# Revit family: Door-Access-Best Access Doors-Insulated-All_Surface_Types-Drywall_Flange-(BA-FRI-DF)
name_source: partatom
category: Specialty Equipment
revit_build: Autodesk Revit 2017 (Build: 20160225_1515(x64)
units: mm (PartAtom-declared; Revit-internal decimal feet)

## family parameters
Cut with Voids When Loaded = No
Host = Face
OmniClass Number = 23.30.10.27.17
Part Type = Normal
Room Calculation Point = No
Round Connector Dimension = Use Diameter
Shared = No

## types (17) — shared parameters
Assembly Code = C1020700
Ceiling Constraint = Maximum dimensions for ceiling mounted panels are 24W x 36H.
Ceiling Mounted = No
Construction Material = Metal - Best Access Doors - Aluminum
Default Elevation = 0"
Description = Fire rated insulated access door with drywall flange
Finish = Metal - Best Access Doors - Powder Coated White
Frame Depth = 2 1/4"
Manufacturer = Best Access Doors
Model = BA-FRI-DF
Product data url = https://bimobject.com
URL = https://www.bestaccessdoors.com
Wall Mounted = Yes

## per-type parameters (varying)
| type | Door Height | Door Height Calc | Door Width | Door Width Calc | Height Actual | Width Actual |
| 8 x 8 | 8" | 8" | 8" | 8" | 10 5/8" | 10 5/8" |
| Custom | 24" | 24" | 24" | 24" | 26 5/8" | 26 5/8" |
| 48 x 48 | 48" | 48" | 48" | 48" | 50 5/8" | 50 5/8" |
| 36 x 36 | 36" | 36" | 36" | 36" | 38 5/8" | 38 5/8" |
| 32 x 32 | 32" | 32" | 32" | 32" | 34 5/8" | 34 5/8" |
| 30 x 30 | 30" | 30" | 30" | 30" | 32 5/8" | 32 5/8" |
| 24 x 48 | 48" | 48" | 24" | 24" | 50 5/8" | 26 5/8" |
| 24 x 36 | 36" | 36" | 24" | 24" | 38 5/8" | 26 5/8" |
| 24 x 24 | 24" | 24" | 24" | 24" | 26 5/8" | 26 5/8" |
| 22 x 36 | 36" | 36" | 22" | 22" | 38 5/8" | 24 5/8" |
| 22 x 30 | 30" | 30" | 22" | 22" | 32 5/8" | 24 5/8" |
| 22 x 22 | 22" | 22" | 22" | 22" | 24 5/8" | 24 5/8" |
| 18 x 18 | 18" | 18" | 18" | 18" | 20 5/8" | 20 5/8" |
| 16 x 16 | 16" | 16" | 16" | 16" | 18 5/8" | 18 5/8" |
| 14 x 14 | 14" | 14" | 14" | 14" | 16 5/8" | 16 5/8" |
| 12 x 12 | 12" | 12" | 12" | 12" | 14 5/8" | 14 5/8" |
| 10 x 10 | 10" | 10" | 10" | 10" | 12 5/8" | 12 5/8" |

## geometry (parser evidence)
native form markers: Blend x4, Sweep x26
no freeform markers — native parametric forms only
